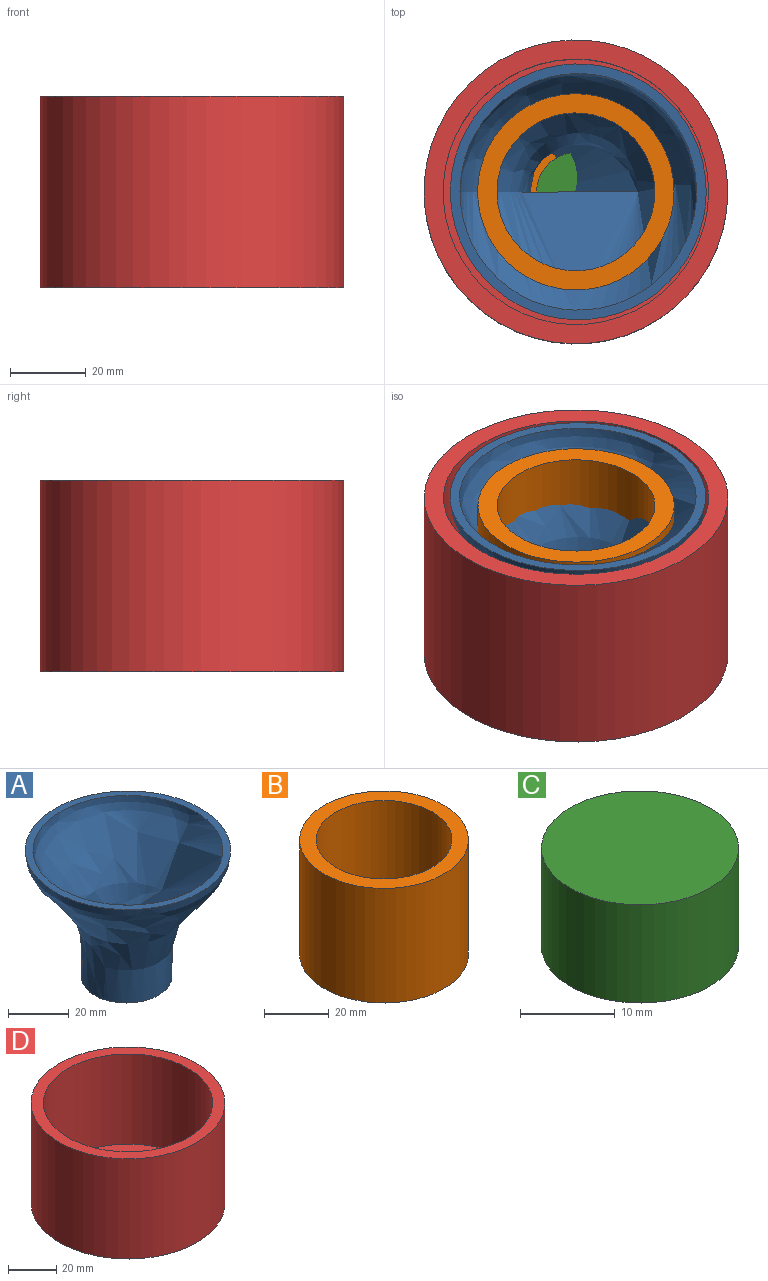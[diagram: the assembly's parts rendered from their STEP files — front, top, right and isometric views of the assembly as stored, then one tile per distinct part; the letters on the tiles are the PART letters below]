
ASSEMBLY  parts=4 mates=3
PART A: 5 faces, bbox 458x374.7x324 mm
  f0: plane 29.83x29.83mm, normal (0,0,-1), area 698.9mm2, adj f2
  f1: plane 340.98x340.98mm, normal (0,0,1), area 521.3mm2, adj f2,f4
  f2: bspline ~67.73x67.73mm, area 7601.7mm2, adj f0,f1
  f3: plane 146.53x146.53mm, normal (0,0,1), area 479.3mm2, adj f4
  f4: offset ~189.81x104.59mm, area 11465.7mm2, adj f1,f3
PART B: 5 faces, bbox 52x52x43.2 mm
  f0: cylinder r=25.99mm len=51.98mm, axis (0,0,-1), area 7050.8mm2, adj f1,f2
  f1: plane 51.98x51.98mm, normal (0,0,1), area 748.4mm2, adj f0,f3
  f2: plane 51.98x51.98mm, normal (0,0,-1), area 2121.8mm2, adj f0
  f3: cylinder r=20.91mm len=41.82mm, axis (0,0,-1), area 5005.2mm2, adj f1,f4
  f4: plane 41.82x41.82mm, normal (0,0,1), area 1373.4mm2, adj f3
PART C: 3 faces, bbox 20.8x20.8x12.7 mm
  f0: cylinder r=10.42mm len=20.84mm, axis (0,0,-1), area 831.3mm2, adj f1,f2
  f1: plane 20.84x20.84mm, normal (0,0,1), area 341mm2, adj f0
  f2: plane 20.84x20.84mm, normal (0,0,-1), area 341mm2, adj f0
PART D: 5 faces, bbox 80.4x80.4x50.8 mm
  f0: cylinder r=40.22mm len=80.44mm, axis (0,0,-1), area 12836.9mm2, adj f1,f2
  f1: plane 80.44x80.44mm, normal (0,0,1), area 1202.6mm2, adj f0,f3
  f2: plane 80.44x80.44mm, normal (0,0,-1), area 5081.4mm2, adj f0
  f3: cylinder r=35.14mm len=70.28mm, axis (0,0,-1), area 10093.9mm2, adj f1,f4
  f4: plane 70.28x70.28mm, normal (0,0,1), area 3878.8mm2, adj f3
PLACE A rot(axis=(0.96,-0.29,0.08),0deg) t=(55.7,65.55,-1.29)mm
PLACE B rot(axis=(0.96,-0.29,0.08),0deg) t=(16.11,65.55,3.79)mm
PLACE C rot(axis=(0.96,-0.29,0.08),0deg) t=(16.11,65.55,-1.29)mm
PLACE D rot(axis=(0.96,-0.29,0.08),0deg) t=(158,57.98,-1.29)mm
MATE fastened D.f0 <-> B.f0  axis (0,0,1) through (16.11,65.55,3.79)mm
MATE fastened C.f0 <-> A.f0  axis (0,0,1) through (16.11,65.55,-1.29)mm
MATE fastened D.f0 <-> C.f0  axis (0,0,-1) through (16.11,65.55,-1.29)mm
